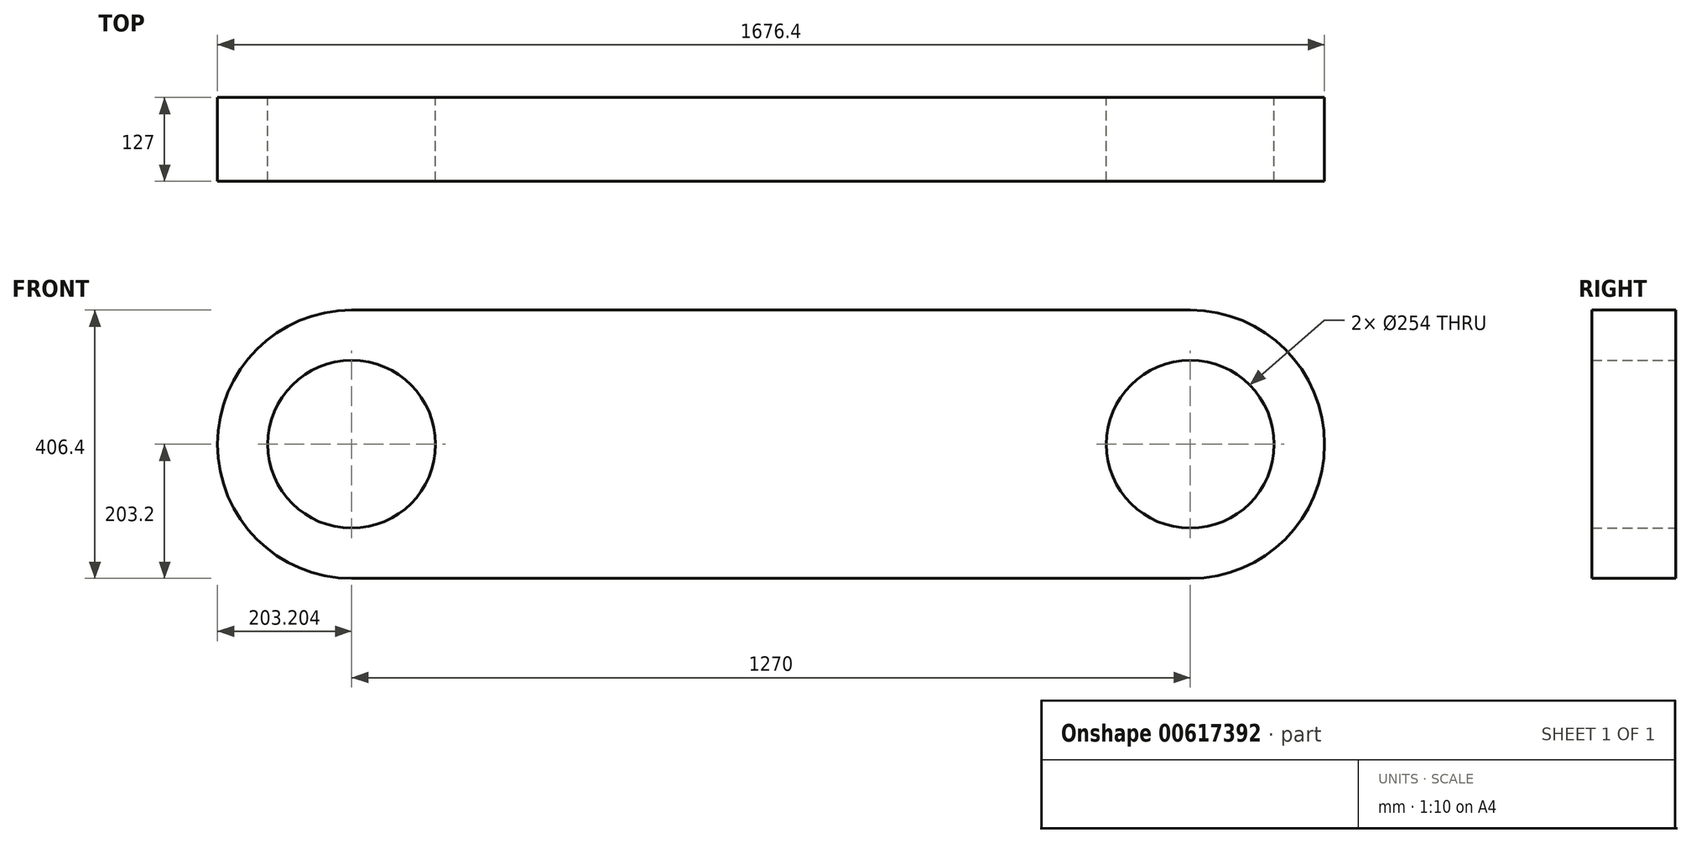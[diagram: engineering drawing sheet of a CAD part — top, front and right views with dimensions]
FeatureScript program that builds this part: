
annotation { "Feature Type Name" : "Feature", "Feature Type Description" : "" }
export const myFeature = defineFeature(function(context is Context, id is Id, definition is map)
    precondition{}
    {
        {
            var Q0;
            Q0=qCreatedBy(makeId("Front.planeOp"),FACE);
            var sketch = newSketch(context, id + "F0", { "sketchPlane" : qUnion([Q0])});
            skLineSegment(sketch, "E0.bottom", {"start": v(-629.98, 203.2) * mm, "end": v(640.02, 203.2) * mm});
            skLineSegment(sketch, "E0.top", {"start": v(-629.98, -203.2) * mm, "end": v(640.02, -203.2) * mm});
            skArc(sketch, "E1", {"start": v(-629.98, 203.2) * mm, "mid": v(-833.18, 0) * mm, "end": v(-629.98, -203.2) * mm});
            skArc(sketch, "E2", {"start": v(640.02, -203.2) * mm, "mid": v(843.22, 0) * mm, "end": v(640.02, 203.2) * mm});
            skCircle(sketch, "E3", {"center": v(-629.98, 0) * mm, "radius": 127 * mm});
            skCircle(sketch, "E4", {"center": v(640.02, 0) * mm, "radius": 127 * mm});
            skSolve(sketch);
        }
        {
            var Q0;
            Q0 = qSketchRegion(id + "F0", true);
            extrude(context, id + "F1", {"entities" : qUnion([Q0]), "endBound" : BoundingType.SYMMETRIC, "depth" : 127 * mm, "offsetDistance" : 25.4 * mm});
        }
    });
